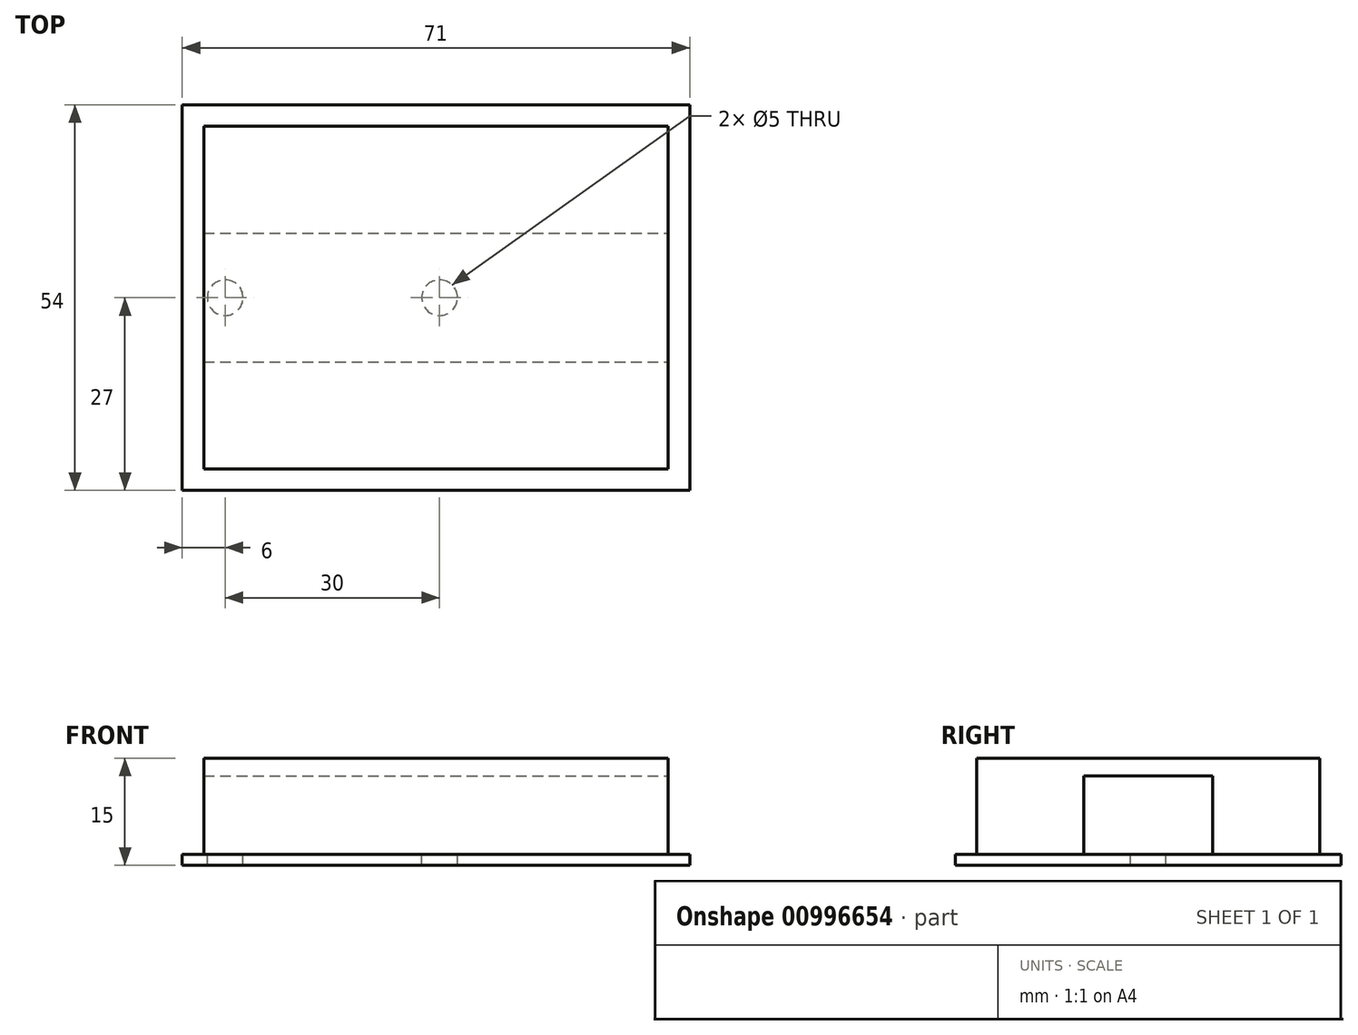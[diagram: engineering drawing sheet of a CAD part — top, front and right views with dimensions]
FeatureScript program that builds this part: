
annotation { "Feature Type Name" : "Feature", "Feature Type Description" : "" }
export const myFeature = defineFeature(function(context is Context, id is Id, definition is map)
    precondition{}
    {
        {
            var Q0;
            Q0=qCreatedBy(makeId("Top.planeOp"),FACE);
            var sketch = newSketch(context, id + "F0", { "sketchPlane" : qUnion([Q0])});
            skLineSegment(sketch, "E0.bottom", {"start": v(35.5, 27) * mm, "end": v(-35.5, 27) * mm});
            skLineSegment(sketch, "E0.top", {"start": v(35.5, -27) * mm, "end": v(-35.5, -27) * mm});
            skLineSegment(sketch, "E0.left", {"start": v(35.5, 27) * mm, "end": v(35.5, -27) * mm});
            skLineSegment(sketch, "E0.right", {"start": v(-35.5, 27) * mm, "end": v(-35.5, -27) * mm});
            skPoint(sketch, "E0.middle", {"position": v(0, 0) * mm});
            skSolve(sketch);
        }
        {
            var Q0;
            Q0 = qSketchRegion(id + "F0", true);
            extrude(context, id + "F1", {"entities" : qUnion([Q0]), "depth" : 1.5 * mm, "offsetDistance" : 25 * mm});
        }
        {
            var Q0;
            Q0=makeQuery(id+"F1.opExtrude","CAP_FACE",FACE,{"disambiguationData":[OSD([sQuery(id+"F0.wireOp",EDGE,"E0.bottom"),sQuery(id+"F0.wireOp",EDGE,"E0.top"),sQuery(id+"F0.wireOp",EDGE,"E0.left"),sQuery(id+"F0.wireOp",EDGE,"E0.right")])],"isStart":false});
            var sketch = newSketch(context, id + "F2", { "sketchPlane" : qUnion([Q0])});
            skLineSegment(sketch, "E1", {"start": v(-35.5, 0) * mm, "end": v(35.5, 0) * mm, "construction": true});
            skCircle(sketch, "E2", {"center": v(-29.5, 0) * mm, "radius": 2.5 * mm});
            skCircle(sketch, "E3", {"center": v(0.5, 0) * mm, "radius": 2.5 * mm});
            skSolve(sketch);
        }
        {
            var Q0;
            Q0 = qSketchRegion(id + "F2", true);
            extrude(context, id + "F3", {"entities" : qUnion([Q0]), "operationType" : NewBodyOperationType.REMOVE, "oppositeDirection" : true, "depth" : 25 * mm, "offsetDistance" : 25 * mm});
        }
        {
            var Q0;
            Q0=makeQuery(id+"F1.opExtrude","CAP_FACE",FACE,{"disambiguationData":[OSD([sQuery(id+"F0.wireOp",EDGE,"E0.bottom"),sQuery(id+"F0.wireOp",EDGE,"E0.top"),sQuery(id+"F0.wireOp",EDGE,"E0.left"),sQuery(id+"F0.wireOp",EDGE,"E0.right")])],"isStart":false});
            var sketch = newSketch(context, id + "F4", { "sketchPlane" : qUnion([Q0])});
            skLineSegment(sketch, "E4.bottom", {"start": v(-32.5, 24) * mm, "end": v(32.5, 24) * mm});
            skLineSegment(sketch, "E4.top", {"start": v(-32.5, 9) * mm, "end": v(32.5, 9) * mm});
            skLineSegment(sketch, "E4.left", {"start": v(-32.5, 24) * mm, "end": v(-32.5, 9) * mm});
            skLineSegment(sketch, "E4.right", {"start": v(32.5, 24) * mm, "end": v(32.5, 9) * mm});
            skLineSegment(sketch, "E5", {"start": v(0, 0) * mm, "end": v(-29.5, 0) * mm, "construction": true});
            skLineSegment(sketch, "E6.MirrorCS", {"start": v(32.5, -24) * mm, "end": v(32.5, -9) * mm});
            skLineSegment(sketch, "E7.MirrorCS", {"start": v(-32.5, -24) * mm, "end": v(32.5, -24) * mm});
            skLineSegment(sketch, "E8.MirrorCS", {"start": v(-32.5, -9) * mm, "end": v(32.5, -9) * mm});
            skLineSegment(sketch, "E9.MirrorCS", {"start": v(-32.5, -24) * mm, "end": v(-32.5, -9) * mm});
            skSolve(sketch);
        }
        {
            var Q0;
            Q0 = qSketchRegion(id + "F4", true);
            extrude(context, id + "F5", {"entities" : qUnion([Q0]), "operationType" : NewBodyOperationType.ADD, "depth" : 11 * mm, "offsetDistance" : 25 * mm});
        }
        {
            var Q0;
            Q0=makeQuery(id+"F5.opExtrude","CAP_FACE",FACE,{"disambiguationData":[OSD([sQuery(id+"F4.wireOp",EDGE,"E4.bottom"),sQuery(id+"F4.wireOp",EDGE,"E4.top"),sQuery(id+"F4.wireOp",EDGE,"E4.left"),sQuery(id+"F4.wireOp",EDGE,"E4.right")])],"isStart":false});
            var sketch = newSketch(context, id + "F6", { "sketchPlane" : qUnion([Q0])});
            skLineSegment(sketch, "E10.bottom", {"start": v(-32.5, 24) * mm, "end": v(32.5, 24) * mm});
            skLineSegment(sketch, "E10.top", {"start": v(-32.5, -24) * mm, "end": v(32.5, -24) * mm});
            skLineSegment(sketch, "E10.left", {"start": v(-32.5, 24) * mm, "end": v(-32.5, -24) * mm});
            skLineSegment(sketch, "E10.right", {"start": v(32.5, 24) * mm, "end": v(32.5, -24) * mm});
            skSolve(sketch);
        }
        {
            var Q0;
            Q0 = qSketchRegion(id + "F6", true);
            extrude(context, id + "F7", {"entities" : qUnion([Q0]), "operationType" : NewBodyOperationType.ADD, "depth" : 2.5 * mm, "offsetDistance" : 25 * mm});
        }
    });
